FCSTD DOCUMENT  (FreeCAD 0.20R)
Label: test_pinned_member
License: All rights reserved
LicenseURL: http://en.wikipedia.org/wiki/All_rights_reserved
objects: Part::FeaturePython×8, App::MaterialObjectPython×1, App::DocumentObjectGroupPython×1, App::DocumentObjectGroup×1
note: 8 computed .brp shape members not serialized (recipe doc carries the construction recipe); baked Part::Feature solids carry a one-line shape summary decoded from their .brp

FEATURE [Part::FeaturePython] Project  # Arch/BIM 0 (typed FeaturePython)
  GlobalId = 0QjBRF7yLCTh4HRF3GOF1t
  IfcData = attributes={"GlobalId": {"name": "GlobalId", "type": "IfcGloballyUniqueId", "is_enum": false, "enum_values": [], "value": "0QjBRF7y... (+404 chars omitted),+1 more (map truncated)
  IfcType = 0
  LongName = Project
FEATURE [Part::FeaturePython] Component  label="Column #1"  # Arch/BIM 135 (typed FeaturePython)
  GlobalId = 3eXlZ8csrAvfIIXVwC_gVP
  HorizontalArea = 0
  IfcData = IfcUID=3eXlZ8csrAvfIIXVwC_gVP,+2 more (map truncated)
  IfcType = 135
  MoveBase = false
  MoveWithHost = false
  PerimeterLength = 0
  PredefinedType = 0
  VerticalArea = 0
FEATURE [Part::FeaturePython] Component001  label="Column #2"  # Arch/BIM 135 (typed FeaturePython)
  GlobalId = 3jULd7ui93JOXl5trkpgTT
  HorizontalArea = 0
  IfcData = IfcUID=3jULd7ui93JOXl5trkpgTT,+2 more (map truncated)
  IfcType = 135
  MoveBase = false
  MoveWithHost = false
  PerimeterLength = 0
  PredefinedType = 0
  VerticalArea = 0
FEATURE [Part::FeaturePython] Component002  label="Lintel"  # Arch/BIM 135 (typed FeaturePython)
  GlobalId = 25vEW7EzrBTvz5cbNWzhP$
  HorizontalArea = 0
  IfcData = IfcUID=25vEW7EzrBTvz5cbNWzhP$,+2 more (map truncated)
  IfcType = 135
  MoveBase = false
  MoveWithHost = false
  PerimeterLength = 0
  PredefinedType = 1
  VerticalArea = 0
FEATURE [App::MaterialObjectPython] Material  label="ASTM A36"  # material (typed FeaturePython)
  Description = ASTM A36
  Material = Description=ASTM A36; Name=ASTM A36; SectionColor=(0.0, 0.0, 0.0); Transparency=0
  Transparency = 0
FEATURE [App::DocumentObjectGroupPython] MaterialContainer  label="Materials"  # scripted group (container) (typed FeaturePython)
  Group = -> [Material]
FEATURE [Part::FeaturePython] Point  # WARN: FeaturePython — macro-defined, semantics opaque (R4)
  X = 0
  Y = 0
  Z = 0
FEATURE [Part::FeaturePython] Point001  # WARN: FeaturePython — macro-defined, semantics opaque (R4)
  Placement = pos=(4876.8,0,0) rot=(0,0,1;0rad)
  X = 4876.8
  Y = 0
  Z = 0
FEATURE [Part::FeaturePython] Component003  label="Support #1"  # Arch/BIM 144 (typed FeaturePython)
  Base = -> Point
  GlobalOrLocal = 0
  HorizontalArea = 0
  IfcData = attributes={"GlobalId": {"name": "GlobalId", "type": "IfcGloballyUniqueId", "is_enum": false, "enum_values": []}, "Description": {"... (+707 chars omitted),+1 more (map truncated)
  IfcType = 144
  MoveBase = false
  MoveWithHost = false
  PerimeterLength = 0
  VerticalArea = 0
FEATURE [Part::FeaturePython] Component004  label="Support #2"  # Arch/BIM 144 (typed FeaturePython)
  Base = -> Point001
  GlobalOrLocal = 0
  HorizontalArea = 0
  IfcData = attributes={"GlobalId": {"name": "GlobalId", "type": "IfcGloballyUniqueId", "is_enum": false, "enum_values": []}, "Description": {"... (+707 chars omitted),+1 more (map truncated)
  IfcType = 144
  MoveBase = false
  MoveWithHost = false
  PerimeterLength = 0
  Placement = pos=(4876.8,0,0) rot=(0,0,1;0rad)
  VerticalArea = 0
FEATURE [App::DocumentObjectGroup] AnalysisModel
  Group = -> [Component,Component001,Component002,Component003,Component004]
